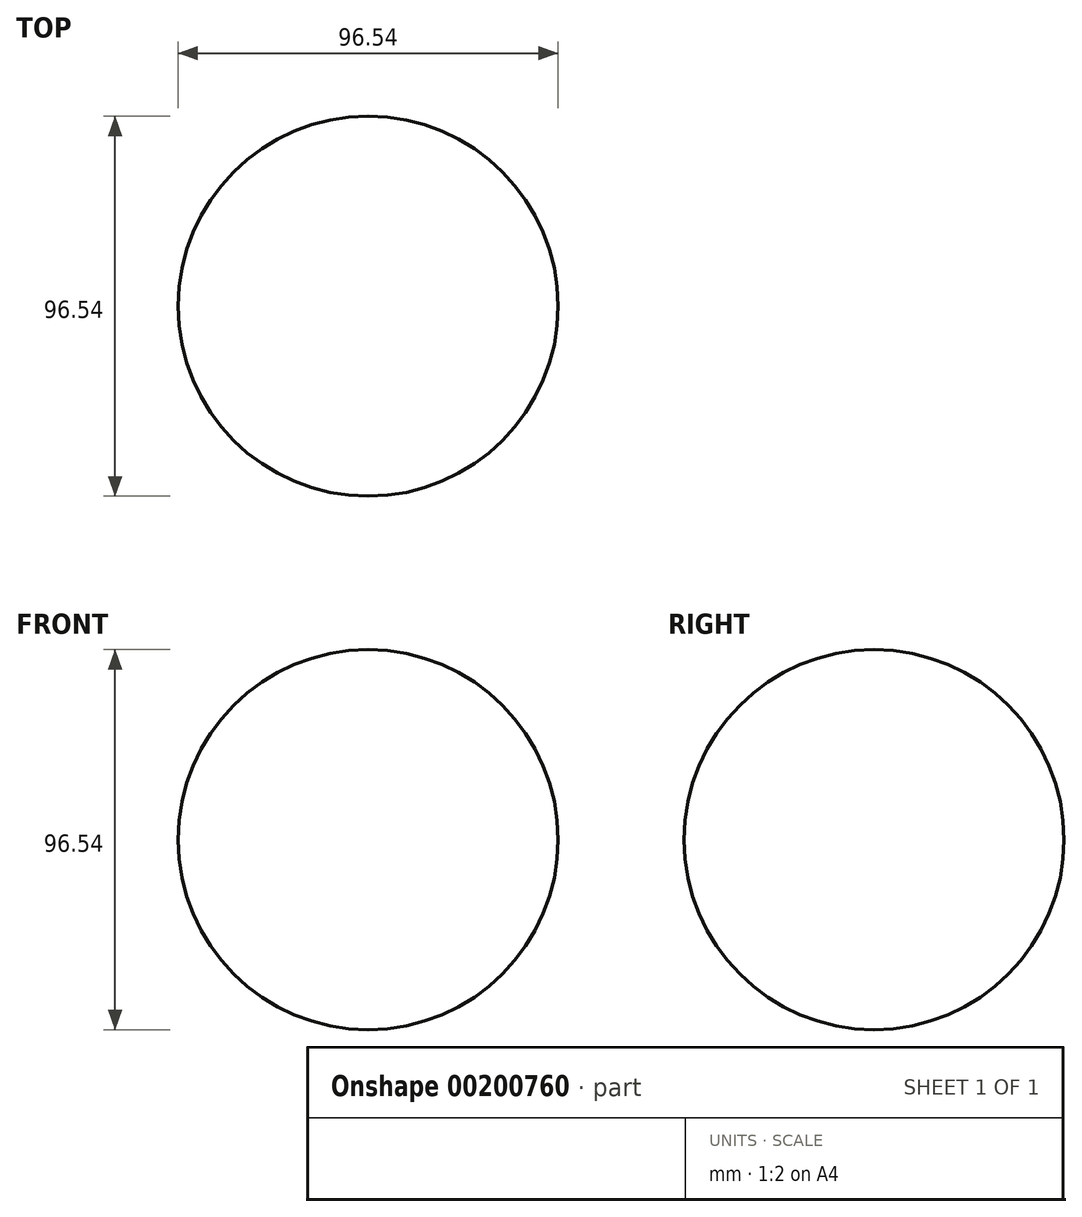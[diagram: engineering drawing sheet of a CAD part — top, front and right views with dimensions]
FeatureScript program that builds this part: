
annotation { "Feature Type Name" : "Feature", "Feature Type Description" : "" }
export const myFeature = defineFeature(function(context is Context, id is Id, definition is map)
    precondition{}
    {
        {
            var Q0;
            Q0=qCreatedBy(makeId("Top.planeOp"),FACE);
            var sketch = newSketch(context, id + "F0", { "sketchPlane" : qUnion([Q0])});
            skArc(sketch, "E0", {"start": v(0, -48.27) * mm, "mid": v(48.27, 0) * mm, "end": v(0, 48.27) * mm});
            skLineSegment(sketch, "E1", {"start": v(0, 48.27) * mm, "end": v(0, -48.27) * mm});
            skSolve(sketch);
        }
        {
            var Q0;
            Q0=makeQuery(id+"F0.imprint","IMPRINT",FACE,{"disambiguationData":[TD([[makeQuery(id+"F0.imprint","IMPRINT",EDGE,{"derivedFrom":sQuery(id+"F0.wireOp",EDGE,"E0")}),1.0]])]});
            var Q1;
            Q1=sQuery(id+"F0.wireOp",EDGE,"E1");
            revolve(context, id + "F1", {"entities" : qUnion([Q0]), "axis" : qUnion([Q1]), "revolveType" : RevolveType.FULL});
        }
    });
